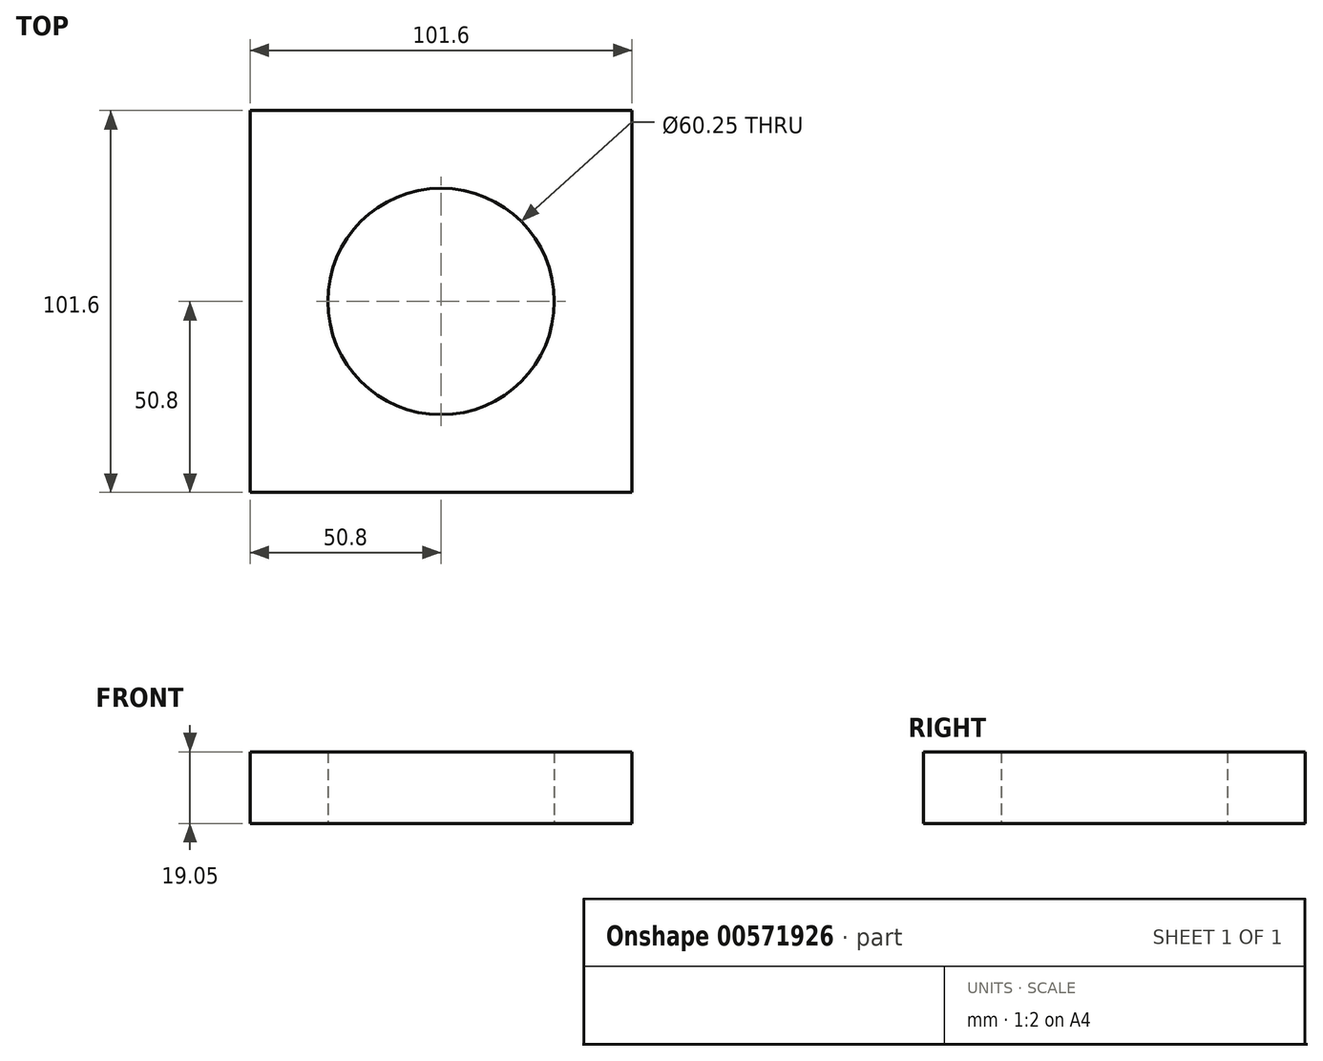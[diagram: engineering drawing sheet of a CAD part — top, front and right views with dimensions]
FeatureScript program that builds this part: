
annotation { "Feature Type Name" : "Feature", "Feature Type Description" : "" }
export const myFeature = defineFeature(function(context is Context, id is Id, definition is map)
    precondition{}
    {
        {
            var Q0;
            Q0=qCreatedBy(makeId("Top.planeOp"),FACE);
            var sketch = newSketch(context, id + "F0", { "sketchPlane" : qUnion([Q0])});
            skLineSegment(sketch, "E0.bottom", {"start": v(0, 0) * mm, "end": v(-101.6, 0) * mm});
            skLineSegment(sketch, "E0.top", {"start": v(0, -101.6) * mm, "end": v(-101.6, -101.6) * mm});
            skLineSegment(sketch, "E0.left", {"start": v(0, 0) * mm, "end": v(0, -101.6) * mm});
            skLineSegment(sketch, "E0.right", {"start": v(-101.6, 0) * mm, "end": v(-101.6, -101.6) * mm});
            skCircle(sketch, "E1", {"center": v(-50.8, -50.8) * mm, "radius": 30.12 * mm});
            skSolve(sketch);
        }
        {
            var Q0;
            Q0=makeQuery(id+"F0.imprint","IMPRINT",FACE,{"disambiguationData":[TD([[makeQuery(id+"F0.imprint","IMPRINT",EDGE,{"derivedFrom":sQuery(id+"F0.wireOp",EDGE,"E0.bottom")}),1.0]])]});
            extrude(context, id + "F1", {"entities" : qUnion([Q0]), "depth" : 19.05 * mm, "offsetDistance" : 25.4 * mm});
        }
    });
